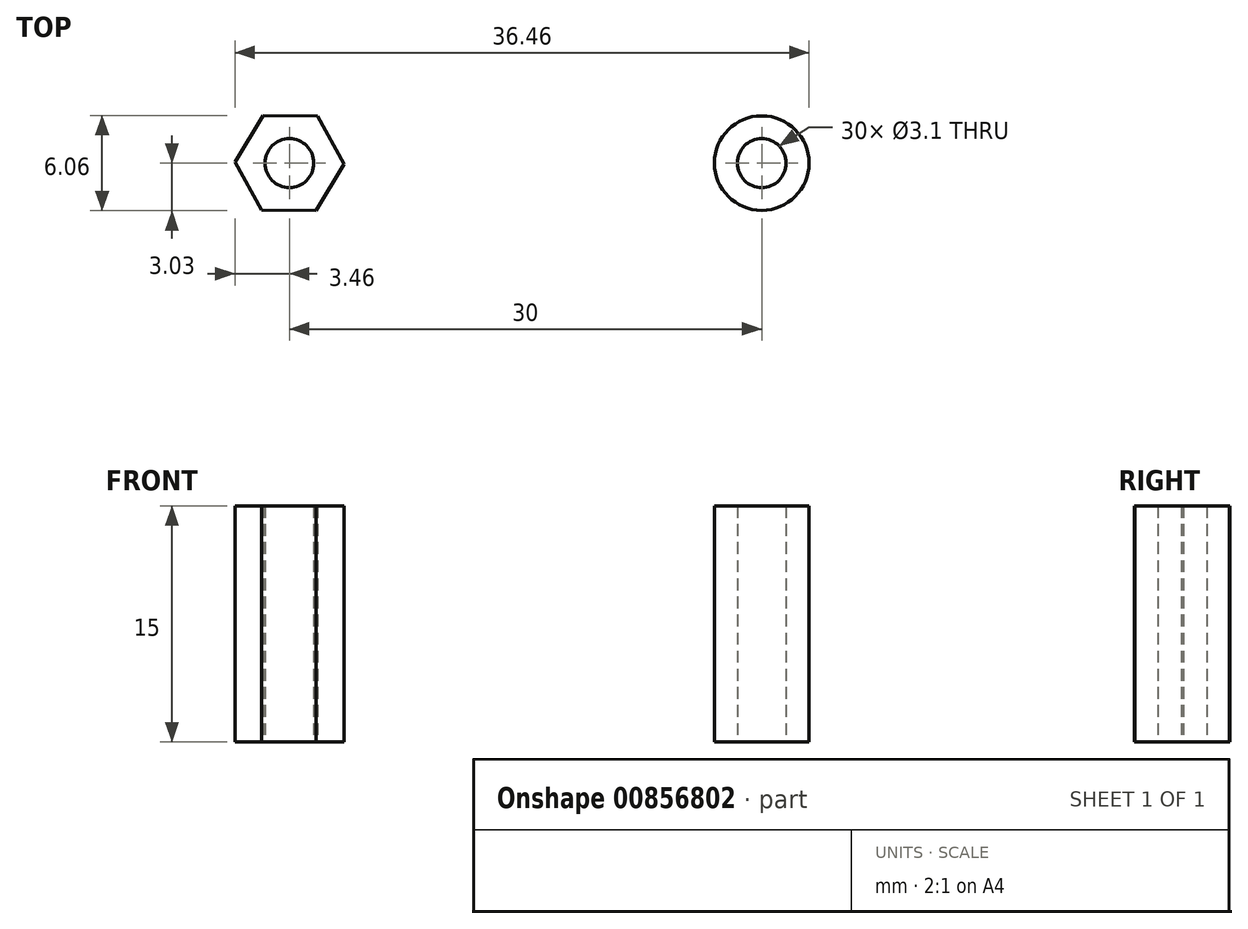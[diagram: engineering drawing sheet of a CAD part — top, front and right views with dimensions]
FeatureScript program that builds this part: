
annotation { "Feature Type Name" : "Feature", "Feature Type Description" : "" }
export const myFeature = defineFeature(function(context is Context, id is Id, definition is map)
    precondition{}
    {
        {
            var Q0;
            Q0=qCreatedBy(makeId("Top.planeOp"),FACE);
            var sketch = newSketch(context, id + "F0", { "sketchPlane" : qUnion([Q0])});
            skCircle(sketch, "E0", {"center": v(0, 0) * mm, "radius": 3 * mm});
            skCircle(sketch, "E1", {"center": v(0, 0) * mm, "radius": 1.55 * mm});
            skCircle(sketch, "E2.cCircle", {"center": v(-30, 0) * mm, "radius": 3 * mm, "construction": true});
            skLineSegment(sketch, "E2.0", {"start": v(-26.54, -0.06) * mm, "end": v(-28.32, -3.03) * mm});
            skLineSegment(sketch, "E2.1", {"start": v(-28.32, -3.03) * mm, "end": v(-31.78, -2.97) * mm});
            skLineSegment(sketch, "E2.2", {"start": v(-31.78, -2.97) * mm, "end": v(-33.46, 0.06) * mm});
            skLineSegment(sketch, "E2.3", {"start": v(-33.46, 0.06) * mm, "end": v(-31.68, 3.03) * mm});
            skLineSegment(sketch, "E2.4", {"start": v(-31.68, 3.03) * mm, "end": v(-28.22, 2.97) * mm});
            skLineSegment(sketch, "E2.5", {"start": v(-28.22, 2.97) * mm, "end": v(-26.54, -0.06) * mm});
            skPoint(sketch, "E2.0.midPoint", {"position": v(-27.43, -1.54) * mm});
            skCircle(sketch, "E3", {"center": v(-30, 0) * mm, "radius": 1.55 * mm});
            skSolve(sketch);
        }
        {
            var Q0;
            Q0=qSketchRegion(id+"F0",true);
            extrude(context, id + "F1", {"entities" : qUnion([Q0]), "depth" : 15 * mm, "offsetDistance" : 25 * mm});
        }
    });
